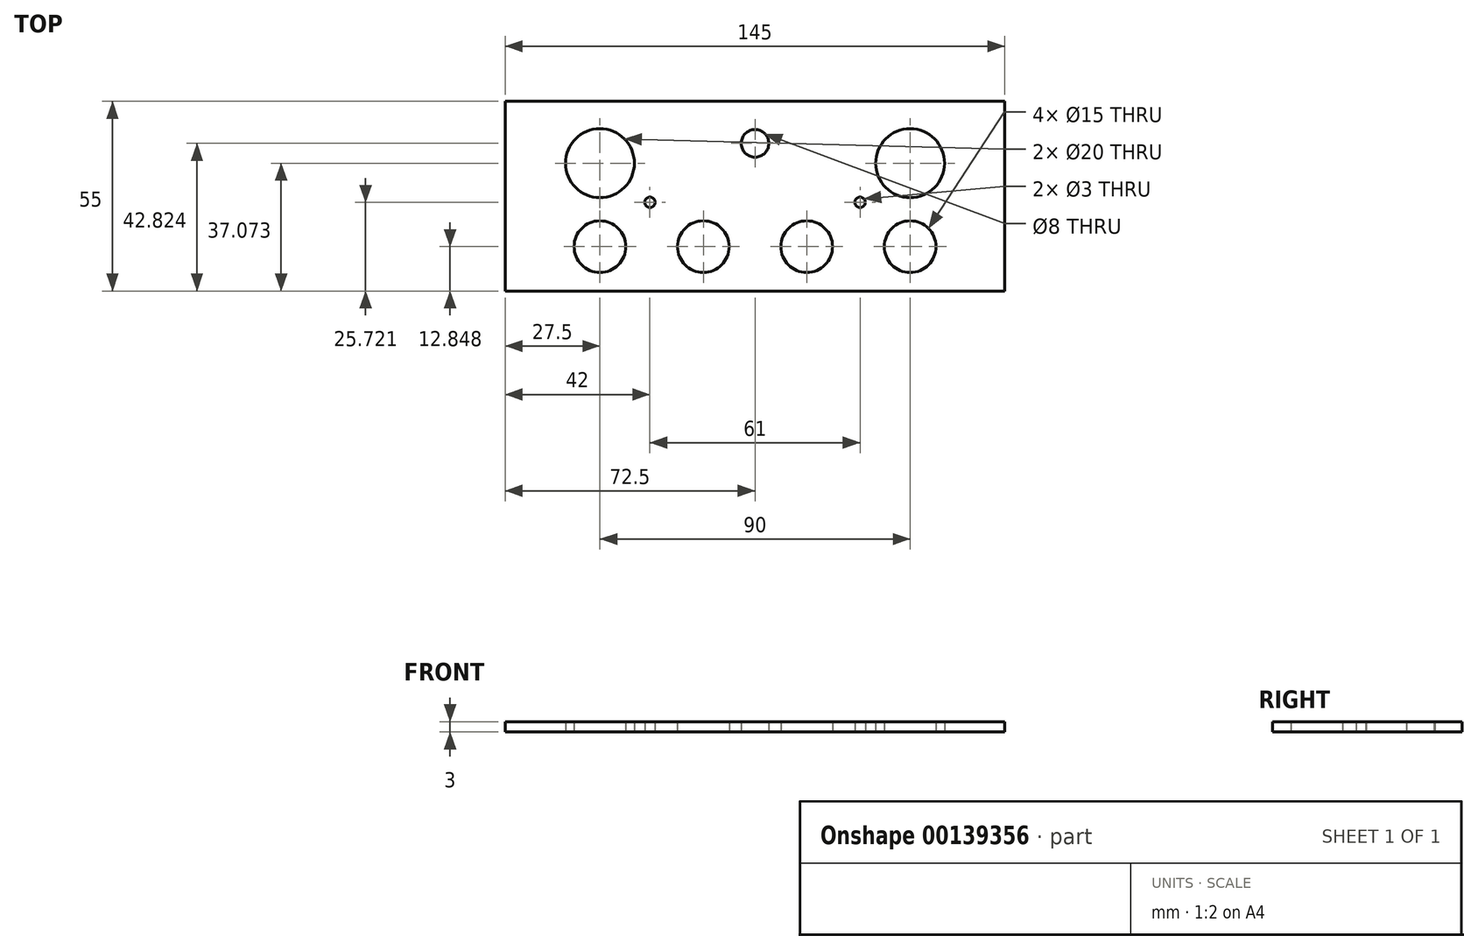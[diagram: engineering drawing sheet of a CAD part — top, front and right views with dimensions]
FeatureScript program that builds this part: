
annotation { "Feature Type Name" : "Feature", "Feature Type Description" : "" }
export const myFeature = defineFeature(function(context is Context, id is Id, definition is map)
    precondition{}
    {
        {
            var Q0;
            Q0=qCreatedBy(makeId("Top.planeOp"),FACE);
            var sketch = newSketch(context, id + "F0", { "sketchPlane" : qUnion([Q0])});
            skLineSegment(sketch, "E0.bottom", {"start": v(0, 0) * mm, "end": v(145, 0) * mm});
            skLineSegment(sketch, "E0.top", {"start": v(0, -55) * mm, "end": v(145, -55) * mm});
            skLineSegment(sketch, "E0.left", {"start": v(0, 0) * mm, "end": v(0, -55) * mm});
            skLineSegment(sketch, "E0.right", {"start": v(145, 0) * mm, "end": v(145, -55) * mm});
            skCircle(sketch, "E1", {"center": v(27.5, -17.93) * mm, "radius": 10 * mm});
            skCircle(sketch, "E2", {"center": v(72.5, -12.18) * mm, "radius": 4 * mm});
            skCircle(sketch, "E3", {"center": v(117.5, -17.93) * mm, "radius": 10 * mm});
            skCircle(sketch, "E4", {"center": v(27.5, -42.15) * mm, "radius": 7.5 * mm});
            skCircle(sketch, "E5", {"center": v(57.5, -42.15) * mm, "radius": 7.5 * mm});
            skCircle(sketch, "E6", {"center": v(117.5, -42.15) * mm, "radius": 7.5 * mm});
            skCircle(sketch, "E7", {"center": v(87.5, -42.15) * mm, "radius": 7.5 * mm});
            skCircle(sketch, "E8", {"center": v(103, -29.28) * mm, "radius": 1.5 * mm});
            skCircle(sketch, "E9", {"center": v(42, -29.28) * mm, "radius": 1.5 * mm});
            skSolve(sketch);
        }
        {
            var Q0;
            Q0 = qSketchRegion(id + "F0", true);
            extrude(context, id + "F1", {"entities" : qUnion([Q0]), "depth" : 3 * mm});
        }
    });
